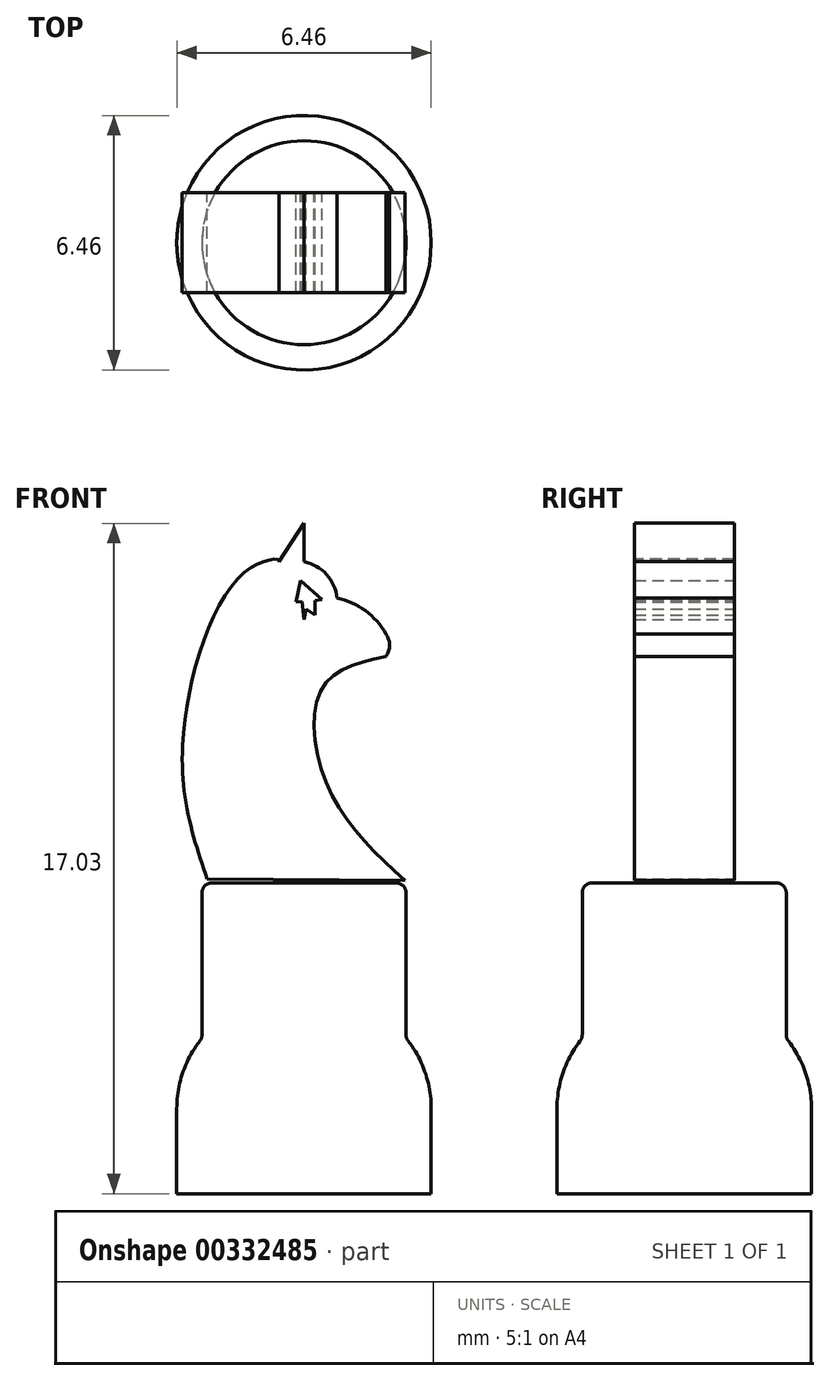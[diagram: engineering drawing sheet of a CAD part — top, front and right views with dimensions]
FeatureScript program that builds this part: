
annotation { "Feature Type Name" : "Feature", "Feature Type Description" : "" }
export const myFeature = defineFeature(function(context is Context, id is Id, definition is map)
    precondition{}
    {
        {
            var Q0;
            Q0=qCreatedBy(makeId("Front.planeOp"),FACE);
            var sketch = newSketch(context, id + "F0", { "sketchPlane" : qUnion([Q0])});
            skLineSegment(sketch, "E0.bottom", {"start": v(0, -19.51) * mm, "end": v(-2.6, -19.51) * mm});
            skLineSegment(sketch, "E0.top", {"start": v(0, -11.61) * mm, "end": v(-2.6, -11.61) * mm});
            skLineSegment(sketch, "E0.left", {"start": v(0, -19.51) * mm, "end": v(0, -11.61) * mm});
            skLineSegment(sketch, "E0.right", {"start": v(-2.6, -19.51) * mm, "end": v(-2.6, -11.61) * mm});
            skLineSegment(sketch, "E1.bottom", {"start": v(-2.6, -15.56) * mm, "end": v(-2.6, -15.56) * mm});
            skLineSegment(sketch, "E1.top", {"start": v(-2.6, -19.51) * mm, "end": v(-2.6, -19.51) * mm});
            skLineSegment(sketch, "E1.left", {"start": v(-2.6, -15.56) * mm, "end": v(-2.6, -19.51) * mm});
            skLineSegment(sketch, "E1.right", {"start": v(-2.6, -15.56) * mm, "end": v(-2.6, -19.51) * mm});
            skLineSegment(sketch, "E2.bottom", {"start": v(-2.6, -15.56) * mm, "end": v(-3.23, -15.56) * mm});
            skLineSegment(sketch, "E2.top", {"start": v(-2.6, -19.51) * mm, "end": v(-3.23, -19.51) * mm});
            skLineSegment(sketch, "E2.right", {"start": v(-3.23, -15.56) * mm, "end": v(-3.23, -19.51) * mm});
            skSolve(sketch);
        }
        {
            var Q0;
            Q0 = qSketchRegion(id + "F0", true);
            var Q1;
            Q1=sQuery(id+"F0.wireOp",EDGE,"E0.left");
            revolve(context, id + "F1", {"entities" : qUnion([Q0]), "axis" : qUnion([Q1]), "revolveType" : RevolveType.FULL});
        }
        {
            var Q0;
            Q0=qCreatedBy(makeId("Front.planeOp"),FACE);
            var sketch = newSketch(context, id + "F2", { "sketchPlane" : qUnion([Q0])});
            skFitSpline(sketch, "E3", {"points": [v(-2.46, -11.51) * mm, v(-3.09, -8.12) * mm, v(-1.52, -3.73) * mm, v(-0.64, -3.41) * mm, v(-0.64, -3.48) * mm], "startDerivative": vector(-2.93, 8.54) * mm, "endDerivative": vector(-0.52, -1.47) * mm});
            skLineSegment(sketch, "E4", {"start": v(-0.63, -3.45) * mm, "end": v(0, -2.48) * mm});
            skLineSegment(sketch, "E5", {"start": v(0, -2.48) * mm, "end": v(0, -3.45) * mm});
            skArc(sketch, "E6", {"start": v(0.84, -4.38) * mm, "mid": v(0.57, -3.78) * mm, "end": v(0, -3.45) * mm});
            skArc(sketch, "E7", {"start": v(2.08, -5.29) * mm, "mid": v(1.56, -4.7) * mm, "end": v(0.84, -4.38) * mm});
            skArc(sketch, "E8", {"start": v(2.08, -5.86) * mm, "mid": v(2.17, -5.57) * mm, "end": v(2.08, -5.29) * mm});
            skLineSegment(sketch, "E9", {"start": v(-2.46, -11.51) * mm, "end": v(2.56, -11.56) * mm});
            skFitSpline(sketch, "E10", {"points": [v(2.56, -11.56) * mm, v(0.62, -9.2) * mm, v(0.48, -6.65) * mm, v(2.08, -5.86) * mm], "startDerivative": vector(-6.07, 5.66) * mm, "endDerivative": vector(6.8, 1.55) * mm});
            skLineSegment(sketch, "E11", {"start": v(2.08, -5.86) * mm, "end": v(-0.63, -3.45) * mm});
            skLineSegment(sketch, "E12", {"start": v(-3.09, -8.12) * mm, "end": v(-0.63, -3.45) * mm});
            skLineSegment(sketch, "E13", {"start": v(0, -3.45) * mm, "end": v(-0.2, -4.48) * mm});
            skLineSegment(sketch, "E14", {"start": v(1.7, -5.57) * mm, "end": v(2.08, -5.29) * mm});
            skLineSegment(sketch, "E15", {"start": v(-0.63, -3.45) * mm, "end": v(0, -3.45) * mm});
            skLineSegment(sketch, "E16", {"start": v(0.84, -4.38) * mm, "end": v(-0.2, -4.48) * mm});
            skLineSegment(sketch, "E17", {"start": v(-0.1, -3.97) * mm, "end": v(0, -4.92) * mm});
            skLineSegment(sketch, "E18", {"start": v(0, -4.92) * mm, "end": v(0.27, -3.55) * mm});
            skLineSegment(sketch, "E19", {"start": v(0.27, -3.55) * mm, "end": v(0.28, -4.81) * mm});
            skLineSegment(sketch, "E20", {"start": v(0.28, -4.81) * mm, "end": v(-0.73, -4.14) * mm});
            skSolve(sketch);
        }
        {
            var Q0;
            Q0 = qSketchRegion(id + "F2", true);
            extrude(context, id + "F3", {"entities" : qUnion([Q0]), "endBound" : BoundingType.SYMMETRIC, "depth" : 2.54 * mm, "offsetDistance" : 25.4 * mm});
        }
        {
            var Q0;
            Q0=makeQuery(id+"F1.opRevolve","SWEPT_EDGE",EDGE,{"disambiguationData":[OSD([sQuery(id+"F0.wireOp",EDGE,"E2.bottom"),sQuery(id+"F0.wireOp",EDGE,"E2.right")])]});
            fillet(context, id + "F4", {"entities" : qUnion([Q0]), "radius" : 2.8 * mm, "tangentPropagation" : true, "allowEdgeOverflow" : false});
        }
        {
            var Q0;
            Q0=makeQuery(id+"F1.opRevolve","SWEPT_FACE",FACE,{"disambiguationData":[OSD([sQuery(id+"F0.wireOp",EDGE,"E0.right")])]});
            fillet(context, id + "F5", {"entities" : qUnion([Q0]), "radius" : 0.25 * mm, "tangentPropagation" : true, "allowEdgeOverflow" : false});
        }
    });
